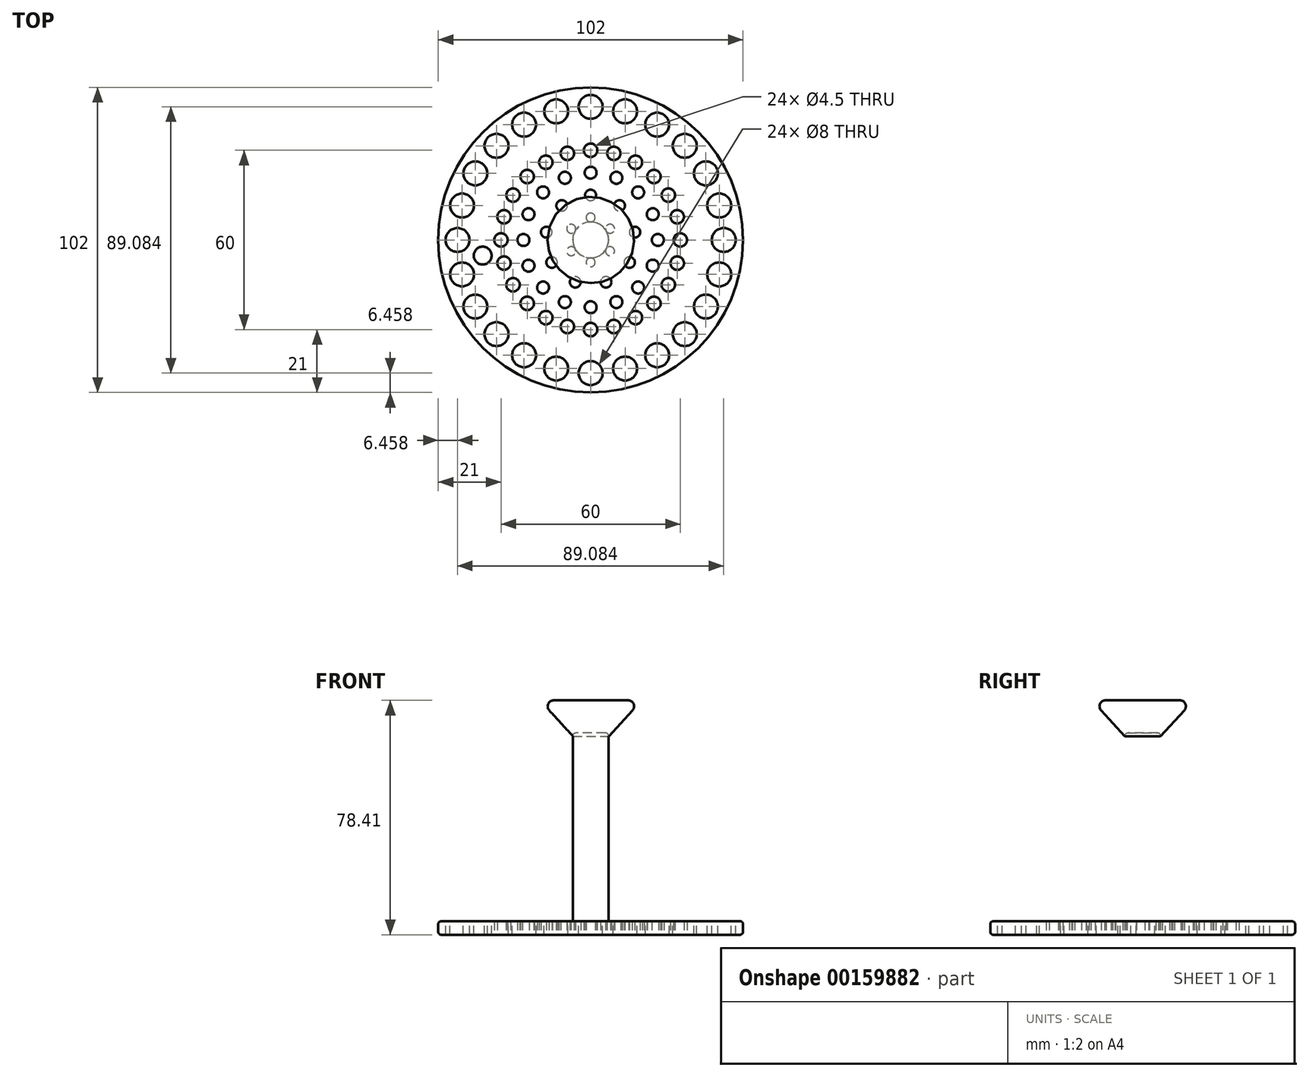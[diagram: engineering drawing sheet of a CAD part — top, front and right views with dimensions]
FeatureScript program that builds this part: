
annotation { "Feature Type Name" : "Feature", "Feature Type Description" : "" }
export const myFeature = defineFeature(function(context is Context, id is Id, definition is map)
    precondition{}
    {
        {
            var Q0;
            Q0=qCreatedBy(makeId("Top.planeOp"),FACE);
            var sketch = newSketch(context, id + "F0", { "sketchPlane" : qUnion([Q0])});
            skCircle(sketch, "E0", {"center": v(0, 0) * mm, "radius": 51 * mm});
            skSolve(sketch);
        }
        {
            var Q0;
            Q0=makeQuery(id+"F0.imprint","IMPRINT",FACE,{"disambiguationData":[TD([[makeQuery(id+"F0.imprint","IMPRINT",EDGE,{"derivedFrom":sQuery(id+"F0.wireOp",EDGE,"E0")}),1.0]])]});
            var sketch = newSketch(context, id + "F1", { "sketchPlane" : qUnion([Q0])});
            skCircle(sketch, "E1", {"center": v(0, 0) * mm, "radius": 7.5 * mm, "construction": true});
            skCircle(sketch, "E2", {"center": v(0, 7.5) * mm, "radius": 1.5 * mm});
            skCircle(sketch, "E3.1.1", {"center": v(-6.5, 3.75) * mm, "radius": 1.5 * mm});
            skCircle(sketch, "E3.2.1", {"center": v(-6.5, -3.75) * mm, "radius": 1.5 * mm});
            skCircle(sketch, "E3.3.1", {"center": v(0, -7.5) * mm, "radius": 1.5 * mm});
            skCircle(sketch, "E3.4.1", {"center": v(6.5, -3.75) * mm, "radius": 1.5 * mm});
            skCircle(sketch, "E3.5.1", {"center": v(6.5, 3.75) * mm, "radius": 1.5 * mm});
            skSolve(sketch);
        }
        {
            var Q0;
            Q0=makeQuery(id+"F0.imprint","IMPRINT",FACE,{"disambiguationData":[TD([[makeQuery(id+"F0.imprint","IMPRINT",EDGE,{"derivedFrom":sQuery(id+"F0.wireOp",EDGE,"E0")}),1.0]])]});
            var sketch = newSketch(context, id + "F2", { "sketchPlane" : qUnion([Q0])});
            skCircle(sketch, "E4", {"center": v(0, 0) * mm, "radius": 15 * mm, "construction": true});
            skCircle(sketch, "E5", {"center": v(0, 15) * mm, "radius": 1.83 * mm});
            skCircle(sketch, "E6.1.0", {"center": v(-9.64, 11.5) * mm, "radius": 1.83 * mm});
            skCircle(sketch, "E6.2.0", {"center": v(-14.77, 2.6) * mm, "radius": 1.83 * mm});
            skCircle(sketch, "E6.3.0", {"center": v(-13, -7.5) * mm, "radius": 1.83 * mm});
            skCircle(sketch, "E6.4.0", {"center": v(-5.13, -14.1) * mm, "radius": 1.83 * mm});
            skCircle(sketch, "E6.5.0", {"center": v(5.13, -14.1) * mm, "radius": 1.83 * mm});
            skCircle(sketch, "E6.6.0", {"center": v(13, -7.5) * mm, "radius": 1.83 * mm});
            skCircle(sketch, "E6.7.0", {"center": v(14.77, 2.6) * mm, "radius": 1.83 * mm});
            skCircle(sketch, "E6.8.0", {"center": v(9.64, 11.5) * mm, "radius": 1.83 * mm});
            skSolve(sketch);
        }
        {
            var Q0;
            Q0=makeQuery(id+"F0.imprint","IMPRINT",FACE,{"disambiguationData":[TD([[makeQuery(id+"F0.imprint","IMPRINT",EDGE,{"derivedFrom":sQuery(id+"F0.wireOp",EDGE,"E0")}),1.0]])]});
            var sketch = newSketch(context, id + "F3", { "sketchPlane" : qUnion([Q0])});
            skCircle(sketch, "E7", {"center": v(0, 0) * mm, "radius": 22.5 * mm, "construction": true});
            skCircle(sketch, "E8", {"center": v(0, 22.5) * mm, "radius": 2 * mm});
            skCircle(sketch, "E9.1.0", {"center": v(-8.61, 20.79) * mm, "radius": 2 * mm});
            skCircle(sketch, "E9.2.0", {"center": v(-15.9, 15.9) * mm, "radius": 2 * mm});
            skCircle(sketch, "E9.3.0", {"center": v(-20.79, 8.61) * mm, "radius": 2 * mm});
            skCircle(sketch, "E9.4.0", {"center": v(-22.5, 0) * mm, "radius": 2 * mm});
            skCircle(sketch, "E9.5.0", {"center": v(-20.79, -8.61) * mm, "radius": 2 * mm});
            skCircle(sketch, "E9.6.0", {"center": v(-15.9, -15.9) * mm, "radius": 2 * mm});
            skCircle(sketch, "E9.7.0", {"center": v(-8.61, -20.79) * mm, "radius": 2 * mm});
            skCircle(sketch, "E9.8.0", {"center": v(0, -22.5) * mm, "radius": 2 * mm});
            skCircle(sketch, "E9.9.0", {"center": v(8.61, -20.79) * mm, "radius": 2 * mm});
            skCircle(sketch, "E9.10.0", {"center": v(15.9, -15.9) * mm, "radius": 2 * mm});
            skCircle(sketch, "E9.11.0", {"center": v(20.79, -8.61) * mm, "radius": 2 * mm});
            skCircle(sketch, "E9.12.0", {"center": v(22.5, 0) * mm, "radius": 2 * mm});
            skCircle(sketch, "E9.13.0", {"center": v(20.79, 8.61) * mm, "radius": 2 * mm});
            skCircle(sketch, "E9.14.0", {"center": v(15.9, 15.9) * mm, "radius": 2 * mm});
            skCircle(sketch, "E9.15.0", {"center": v(8.61, 20.79) * mm, "radius": 2 * mm});
            skSolve(sketch);
        }
        {
            var Q0;
            Q0=makeQuery(id+"F0.imprint","IMPRINT",FACE,{"disambiguationData":[TD([[makeQuery(id+"F0.imprint","IMPRINT",EDGE,{"derivedFrom":sQuery(id+"F0.wireOp",EDGE,"E0")}),1.0]])]});
            var sketch = newSketch(context, id + "F4", { "sketchPlane" : qUnion([Q0])});
            skCircle(sketch, "E10", {"center": v(0, 0) * mm, "radius": 30 * mm, "construction": true});
            skCircle(sketch, "E11", {"center": v(0, 30) * mm, "radius": 2.25 * mm});
            skCircle(sketch, "E12.1.0", {"center": v(-7.76, 28.98) * mm, "radius": 2.25 * mm});
            skCircle(sketch, "E12.2.0", {"center": v(-15, 25.98) * mm, "radius": 2.25 * mm});
            skCircle(sketch, "E13.1.3.0", {"center": v(-21.21, 21.21) * mm, "radius": 2.25 * mm});
            skCircle(sketch, "E13.1.4.0", {"center": v(-25.98, 15) * mm, "radius": 2.25 * mm});
            skCircle(sketch, "E13.1.5.0", {"center": v(-28.98, 7.76) * mm, "radius": 2.25 * mm});
            skCircle(sketch, "E13.1.6.0", {"center": v(-30, 0) * mm, "radius": 2.25 * mm});
            skCircle(sketch, "E13.1.7.0", {"center": v(-28.98, -7.76) * mm, "radius": 2.25 * mm});
            skCircle(sketch, "E13.1.8.0", {"center": v(-25.98, -15) * mm, "radius": 2.25 * mm});
            skCircle(sketch, "E13.1.9.0", {"center": v(-21.21, -21.21) * mm, "radius": 2.25 * mm});
            skCircle(sketch, "E13.1.10.0", {"center": v(-15, -25.98) * mm, "radius": 2.25 * mm});
            skCircle(sketch, "E13.1.11.0", {"center": v(-7.76, -28.98) * mm, "radius": 2.25 * mm});
            skCircle(sketch, "E13.1.12.0", {"center": v(0, -30) * mm, "radius": 2.25 * mm});
            skCircle(sketch, "E13.1.13.0", {"center": v(7.76, -28.98) * mm, "radius": 2.25 * mm});
            skCircle(sketch, "E13.1.14.0", {"center": v(15, -25.98) * mm, "radius": 2.25 * mm});
            skCircle(sketch, "E13.1.15.0", {"center": v(21.21, -21.21) * mm, "radius": 2.25 * mm});
            skCircle(sketch, "E13.1.16.0", {"center": v(25.98, -15) * mm, "radius": 2.25 * mm});
            skCircle(sketch, "E13.1.17.0", {"center": v(28.98, -7.76) * mm, "radius": 2.25 * mm});
            skCircle(sketch, "E13.1.18.0", {"center": v(30, 0) * mm, "radius": 2.25 * mm});
            skCircle(sketch, "E13.1.19.0", {"center": v(28.98, 7.76) * mm, "radius": 2.25 * mm});
            skCircle(sketch, "E13.1.20.0", {"center": v(25.98, 15) * mm, "radius": 2.25 * mm});
            skCircle(sketch, "E13.1.21.0", {"center": v(21.21, 21.21) * mm, "radius": 2.25 * mm});
            skCircle(sketch, "E13.1.22.0", {"center": v(15, 25.98) * mm, "radius": 2.25 * mm});
            skCircle(sketch, "E13.1.23.0", {"center": v(7.76, 28.98) * mm, "radius": 2.25 * mm});
            skSolve(sketch);
        }
        {
            var Q0;
            Q0=qSketchRegion(id+"F4",true);
            extrude(context, id + "F5", {"entities" : qUnion([Q0]), "depth" : 5 * mm});
        }
        {
            var Q0;
            Q0=qSketchRegion(id+"F3",true);
            extrude(context, id + "F6", {"entities" : qUnion([Q0]), "depth" : 5 * mm});
        }
        {
            var Q0;
            Q0=qSketchRegion(id+"F2",true);
            extrude(context, id + "F7", {"entities" : qUnion([Q0]), "depth" : 5 * mm});
        }
        {
            var Q0;
            Q0=qSketchRegion(id+"F1",true);
            extrude(context, id + "F8", {"entities" : qUnion([Q0]), "depth" : 5 * mm});
        }
        {
            var Q0;
            Q0=qSketchRegion(id+"F0",true);
            extrude(context, id + "F9", {"entities" : qUnion([Q0]), "depth" : 4.5 * mm});
        }
        {
            var Q0;
            Q0=makeQuery(id+"F5.opExtrude","SWEPT_BODY",BODY,{"disambiguationData":[OSD([sQuery(id+"F4.wireOp",EDGE,"E11")])]});
            var Q1;
            Q1=makeQuery(id+"F5.opExtrude","SWEPT_BODY",BODY,{"disambiguationData":[OSD([sQuery(id+"F4.wireOp",EDGE,"E13.1.3.0")])]});
            var Q2;
            Q2=makeQuery(id+"F5.opExtrude","SWEPT_BODY",BODY,{"disambiguationData":[OSD([sQuery(id+"F4.wireOp",EDGE,"E13.1.7.0")])]});
            var Q3;
            Q3=makeQuery(id+"F5.opExtrude","SWEPT_BODY",BODY,{"disambiguationData":[OSD([sQuery(id+"F4.wireOp",EDGE,"E12.1.0")])]});
            var Q4;
            Q4=makeQuery(id+"F5.opExtrude","SWEPT_BODY",BODY,{"disambiguationData":[OSD([sQuery(id+"F4.wireOp",EDGE,"E12.2.0")])]});
            var Q5;
            Q5=makeQuery(id+"F5.opExtrude","SWEPT_BODY",BODY,{"disambiguationData":[OSD([sQuery(id+"F4.wireOp",EDGE,"E13.1.4.0")])]});
            var Q6;
            Q6=makeQuery(id+"F5.opExtrude","SWEPT_BODY",BODY,{"disambiguationData":[OSD([sQuery(id+"F4.wireOp",EDGE,"E13.1.5.0")])]});
            var Q7;
            Q7=makeQuery(id+"F5.opExtrude","SWEPT_BODY",BODY,{"disambiguationData":[OSD([sQuery(id+"F4.wireOp",EDGE,"E13.1.6.0")])]});
            var Q8;
            Q8=makeQuery(id+"F5.opExtrude","SWEPT_BODY",BODY,{"disambiguationData":[OSD([sQuery(id+"F4.wireOp",EDGE,"E13.1.8.0")])]});
            var Q9;
            Q9=makeQuery(id+"F5.opExtrude","SWEPT_BODY",BODY,{"disambiguationData":[OSD([sQuery(id+"F4.wireOp",EDGE,"E13.1.9.0")])]});
            var Q10;
            Q10=makeQuery(id+"F5.opExtrude","SWEPT_BODY",BODY,{"disambiguationData":[OSD([sQuery(id+"F4.wireOp",EDGE,"E13.1.10.0")])]});
            var Q11;
            Q11=makeQuery(id+"F5.opExtrude","SWEPT_BODY",BODY,{"disambiguationData":[OSD([sQuery(id+"F4.wireOp",EDGE,"E13.1.11.0")])]});
            var Q12;
            Q12=makeQuery(id+"F5.opExtrude","SWEPT_BODY",BODY,{"disambiguationData":[OSD([sQuery(id+"F4.wireOp",EDGE,"E13.1.12.0")])]});
            var Q13;
            Q13=makeQuery(id+"F5.opExtrude","SWEPT_BODY",BODY,{"disambiguationData":[OSD([sQuery(id+"F4.wireOp",EDGE,"E13.1.13.0")])]});
            var Q14;
            Q14=makeQuery(id+"F5.opExtrude","SWEPT_BODY",BODY,{"disambiguationData":[OSD([sQuery(id+"F4.wireOp",EDGE,"E13.1.14.0")])]});
            var Q15;
            Q15=makeQuery(id+"F5.opExtrude","SWEPT_BODY",BODY,{"disambiguationData":[OSD([sQuery(id+"F4.wireOp",EDGE,"E13.1.15.0")])]});
            var Q16;
            Q16=makeQuery(id+"F5.opExtrude","SWEPT_BODY",BODY,{"disambiguationData":[OSD([sQuery(id+"F4.wireOp",EDGE,"E13.1.16.0")])]});
            var Q17;
            Q17=makeQuery(id+"F5.opExtrude","SWEPT_BODY",BODY,{"disambiguationData":[OSD([sQuery(id+"F4.wireOp",EDGE,"E13.1.17.0")])]});
            var Q18;
            Q18=makeQuery(id+"F5.opExtrude","SWEPT_BODY",BODY,{"disambiguationData":[OSD([sQuery(id+"F4.wireOp",EDGE,"E13.1.18.0")])]});
            var Q19;
            Q19=makeQuery(id+"F5.opExtrude","SWEPT_BODY",BODY,{"disambiguationData":[OSD([sQuery(id+"F4.wireOp",EDGE,"E13.1.19.0")])]});
            var Q20;
            Q20=makeQuery(id+"F5.opExtrude","SWEPT_BODY",BODY,{"disambiguationData":[OSD([sQuery(id+"F4.wireOp",EDGE,"E13.1.20.0")])]});
            var Q21;
            Q21=makeQuery(id+"F5.opExtrude","SWEPT_BODY",BODY,{"disambiguationData":[OSD([sQuery(id+"F4.wireOp",EDGE,"E13.1.21.0")])]});
            var Q22;
            Q22=makeQuery(id+"F5.opExtrude","SWEPT_BODY",BODY,{"disambiguationData":[OSD([sQuery(id+"F4.wireOp",EDGE,"E13.1.22.0")])]});
            var Q23;
            Q23=makeQuery(id+"F5.opExtrude","SWEPT_BODY",BODY,{"disambiguationData":[OSD([sQuery(id+"F4.wireOp",EDGE,"E13.1.23.0")])]});
            var Q24;
            Q24=makeQuery(id+"F6.opExtrude","SWEPT_BODY",BODY,{"disambiguationData":[OSD([sQuery(id+"F3.wireOp",EDGE,"E9.15.0")])]});
            var Q25;
            Q25=makeQuery(id+"F6.opExtrude","SWEPT_BODY",BODY,{"disambiguationData":[OSD([sQuery(id+"F3.wireOp",EDGE,"E8")])]});
            var Q26;
            Q26=makeQuery(id+"F6.opExtrude","SWEPT_BODY",BODY,{"disambiguationData":[OSD([sQuery(id+"F3.wireOp",EDGE,"E9.1.0")])]});
            var Q27;
            Q27=makeQuery(id+"F6.opExtrude","SWEPT_BODY",BODY,{"disambiguationData":[OSD([sQuery(id+"F3.wireOp",EDGE,"E9.2.0")])]});
            var Q28;
            Q28=makeQuery(id+"F6.opExtrude","SWEPT_BODY",BODY,{"disambiguationData":[OSD([sQuery(id+"F3.wireOp",EDGE,"E9.3.0")])]});
            var Q29;
            Q29=makeQuery(id+"F6.opExtrude","SWEPT_BODY",BODY,{"disambiguationData":[OSD([sQuery(id+"F3.wireOp",EDGE,"E9.4.0")])]});
            var Q30;
            Q30=makeQuery(id+"F6.opExtrude","SWEPT_BODY",BODY,{"disambiguationData":[OSD([sQuery(id+"F3.wireOp",EDGE,"E9.5.0")])]});
            var Q31;
            Q31=makeQuery(id+"F6.opExtrude","SWEPT_BODY",BODY,{"disambiguationData":[OSD([sQuery(id+"F3.wireOp",EDGE,"E9.6.0")])]});
            var Q32;
            Q32=makeQuery(id+"F6.opExtrude","SWEPT_BODY",BODY,{"disambiguationData":[OSD([sQuery(id+"F3.wireOp",EDGE,"E9.7.0")])]});
            var Q33;
            Q33=makeQuery(id+"F6.opExtrude","SWEPT_BODY",BODY,{"disambiguationData":[OSD([sQuery(id+"F3.wireOp",EDGE,"E9.8.0")])]});
            var Q34;
            Q34=makeQuery(id+"F6.opExtrude","SWEPT_BODY",BODY,{"disambiguationData":[OSD([sQuery(id+"F3.wireOp",EDGE,"E9.9.0")])]});
            var Q35;
            Q35=makeQuery(id+"F6.opExtrude","SWEPT_BODY",BODY,{"disambiguationData":[OSD([sQuery(id+"F3.wireOp",EDGE,"E9.10.0")])]});
            var Q36;
            Q36=makeQuery(id+"F6.opExtrude","SWEPT_BODY",BODY,{"disambiguationData":[OSD([sQuery(id+"F3.wireOp",EDGE,"E9.11.0")])]});
            var Q37;
            Q37=makeQuery(id+"F6.opExtrude","SWEPT_BODY",BODY,{"disambiguationData":[OSD([sQuery(id+"F3.wireOp",EDGE,"E9.12.0")])]});
            var Q38;
            Q38=makeQuery(id+"F6.opExtrude","SWEPT_BODY",BODY,{"disambiguationData":[OSD([sQuery(id+"F3.wireOp",EDGE,"E9.13.0")])]});
            var Q39;
            Q39=makeQuery(id+"F6.opExtrude","SWEPT_BODY",BODY,{"disambiguationData":[OSD([sQuery(id+"F3.wireOp",EDGE,"E9.14.0")])]});
            var Q40;
            Q40=makeQuery(id+"F7.opExtrude","SWEPT_BODY",BODY,{"disambiguationData":[OSD([sQuery(id+"F2.wireOp",EDGE,"E6.8.0")])]});
            var Q41;
            Q41=makeQuery(id+"F7.opExtrude","SWEPT_BODY",BODY,{"disambiguationData":[OSD([sQuery(id+"F2.wireOp",EDGE,"E6.7.0")])]});
            var Q42;
            Q42=makeQuery(id+"F7.opExtrude","SWEPT_BODY",BODY,{"disambiguationData":[OSD([sQuery(id+"F2.wireOp",EDGE,"E6.6.0")])]});
            var Q43;
            Q43=makeQuery(id+"F7.opExtrude","SWEPT_BODY",BODY,{"disambiguationData":[OSD([sQuery(id+"F2.wireOp",EDGE,"E6.5.0")])]});
            var Q44;
            Q44=makeQuery(id+"F7.opExtrude","SWEPT_BODY",BODY,{"disambiguationData":[OSD([sQuery(id+"F2.wireOp",EDGE,"E6.4.0")])]});
            var Q45;
            Q45=makeQuery(id+"F7.opExtrude","SWEPT_BODY",BODY,{"disambiguationData":[OSD([sQuery(id+"F2.wireOp",EDGE,"E6.3.0")])]});
            var Q46;
            Q46=makeQuery(id+"F7.opExtrude","SWEPT_BODY",BODY,{"disambiguationData":[OSD([sQuery(id+"F2.wireOp",EDGE,"E6.2.0")])]});
            var Q47;
            Q47=makeQuery(id+"F7.opExtrude","SWEPT_BODY",BODY,{"disambiguationData":[OSD([sQuery(id+"F2.wireOp",EDGE,"E6.1.0")])]});
            var Q48;
            Q48=makeQuery(id+"F7.opExtrude","SWEPT_BODY",BODY,{"disambiguationData":[OSD([sQuery(id+"F2.wireOp",EDGE,"E5")])]});
            var Q49;
            Q49=makeQuery(id+"F8.opExtrude","SWEPT_BODY",BODY,{"disambiguationData":[OSD([sQuery(id+"F1.wireOp",EDGE,"E2")])]});
            var Q50;
            Q50=makeQuery(id+"F8.opExtrude","SWEPT_BODY",BODY,{"disambiguationData":[OSD([sQuery(id+"F1.wireOp",EDGE,"E3.5.1")])]});
            var Q51;
            Q51=makeQuery(id+"F8.opExtrude","SWEPT_BODY",BODY,{"disambiguationData":[OSD([sQuery(id+"F1.wireOp",EDGE,"E3.4.1")])]});
            var Q52;
            Q52=makeQuery(id+"F8.opExtrude","SWEPT_BODY",BODY,{"disambiguationData":[OSD([sQuery(id+"F1.wireOp",EDGE,"E3.3.1")])]});
            var Q53;
            Q53=makeQuery(id+"F8.opExtrude","SWEPT_BODY",BODY,{"disambiguationData":[OSD([sQuery(id+"F1.wireOp",EDGE,"E3.2.1")])]});
            var Q54;
            Q54=makeQuery(id+"F8.opExtrude","SWEPT_BODY",BODY,{"disambiguationData":[OSD([sQuery(id+"F1.wireOp",EDGE,"E3.1.1")])]});
            var Q55;
            Q55=makeQuery(id+"F9.opExtrude","SWEPT_BODY",BODY,{"disambiguationData":[OSD([sQuery(id+"F0.wireOp",EDGE,"E0")])]});
            booleanBodies(context, id + "F10", {"operationType" : BooleanOperationType.SUBTRACTION, "tools" : qUnion([Q0, Q1, Q2, Q3, Q4, Q5, Q6, Q7, Q8, Q9, Q10, Q11, Q12, Q13, Q14, Q15, Q16, Q17, Q18, Q19, Q20, Q21, Q22, Q23, Q24, Q25, Q26, Q27, Q28, Q29, Q30, Q31, Q32, Q33, Q34, Q35, Q36, Q37, Q38, Q39, Q40, Q41, Q42, Q43, Q44, Q45, Q46, Q47, Q48, Q49, Q50, Q51, Q52, Q53, Q54]), "targets" : qUnion([Q55])});
        }
        {
            var Q0;
            Q0=makeQuery(id+"F9.opExtrude","CAP_EDGE",EDGE,{"disambiguationData":[OSD([sQuery(id+"F0.wireOp",EDGE,"E0")])],"isStart":true});
            var Q1;
            Q1=makeQuery(id+"F9.opExtrude","CAP_EDGE",EDGE,{"disambiguationData":[OSD([sQuery(id+"F0.wireOp",EDGE,"E0")])],"isStart":false});
            fillet(context, id + "F11", {"entities" : qUnion([Q0, Q1]), "radius" : 1 * mm, "tangentPropagation" : true, "allowEdgeOverflow" : false});
        }
        {
            var Q0;
            Q0=makeQuery(id+"F9.opExtrude","CAP_FACE",FACE,{"disambiguationData":[OSD([sQuery(id+"F0.wireOp",EDGE,"E0")])],"isStart":false});
            var sketch = newSketch(context, id + "F12", { "sketchPlane" : qUnion([Q0])});
            skCircle(sketch, "E14", {"center": v(0, 0) * mm, "radius": 6 * mm});
            skSolve(sketch);
        }
        {
            var Q0;
            Q0=makeQuery(id+"F12.imprint","IMPRINT",FACE,{"disambiguationData":[TD([[makeQuery(id+"F12.imprint","IMPRINT",EDGE,{"derivedFrom":sQuery(id+"F12.wireOp",EDGE,"E14")}),1.0]])]});
            extrude(context, id + "F13", {"entities" : qUnion([Q0]), "operationType" : NewBodyOperationType.ADD, "offsetDistance" : 25 * mm, "depth" : 63 * mm});
        }
        {
            var Q0;
            Q0=makeQuery(id+"F13.opExtrude","CAP_EDGE",EDGE,{"disambiguationData":[OSD([sQuery(id+"F12.wireOp",EDGE,"E14")])],"isStart":false});
            fillet(context, id + "F14", {"entities" : qUnion([Q0]), "radius" : 1 * mm, "tangentPropagation" : true, "allowEdgeOverflow" : false});
        }
        {
            var Q0;
            Q0=makeQuery(id+"F9.opExtrude","CAP_FACE",FACE,{"disambiguationData":[OSD([sQuery(id+"F0.wireOp",EDGE,"E0")])],"isStart":false});
            var sketch = newSketch(context, id + "F15", { "sketchPlane" : qUnion([Q0])});
            skCircle(sketch, "E15", {"center": v(0, 0) * mm, "radius": 36.5 * mm, "construction": true});
            skCircle(sketch, "E16", {"center": v(-36.12, -5.23) * mm, "radius": 3 * mm});
            skSolve(sketch);
        }
        {
            var Q0;
            Q0=makeQuery(id+"F15.imprint","IMPRINT",FACE,{"disambiguationData":[TD([[makeQuery(id+"F15.imprint","IMPRINT",EDGE,{"derivedFrom":sQuery(id+"F15.wireOp",EDGE,"E16")}),1.0]])]});
            extrude(context, id + "F16", {"entities" : qUnion([Q0]), "operationType" : NewBodyOperationType.REMOVE, "oppositeDirection" : true, "offsetDistance" : 25 * mm, "depth" : 25 * mm});
        }
        {
            var Q0;
            Q0=makeQuery(id+"F9.opExtrude","CAP_FACE",FACE,{"disambiguationData":[OSD([sQuery(id+"F0.wireOp",EDGE,"E0")])],"isStart":false});
            var sketch = newSketch(context, id + "F17", { "sketchPlane" : qUnion([Q0])});
            skCircle(sketch, "E17", {"center": v(0, 0) * mm, "radius": 4.85 * mm, "construction": true});
            skCircle(sketch, "E18", {"center": v(0, 0) * mm, "radius": 44.54 * mm, "construction": true});
            skCircle(sketch, "E19", {"center": v(-44.54, 0) * mm, "radius": 4 * mm});
            skCircle(sketch, "E20.1.0", {"center": v(-43.02, -11.53) * mm, "radius": 4 * mm});
            skCircle(sketch, "E20.2.0", {"center": v(-38.57, -22.27) * mm, "radius": 4 * mm});
            skCircle(sketch, "E20.3.0", {"center": v(-31.5, -31.5) * mm, "radius": 4 * mm});
            skCircle(sketch, "E20.4.0", {"center": v(-22.27, -38.57) * mm, "radius": 4 * mm});
            skCircle(sketch, "E20.5.0", {"center": v(-11.53, -43.02) * mm, "radius": 4 * mm});
            skCircle(sketch, "E20.6.0", {"center": v(0, -44.54) * mm, "radius": 4 * mm});
            skCircle(sketch, "E20.7.0", {"center": v(11.53, -43.02) * mm, "radius": 4 * mm});
            skCircle(sketch, "E20.8.0", {"center": v(22.27, -38.57) * mm, "radius": 4 * mm});
            skCircle(sketch, "E20.9.0", {"center": v(31.5, -31.5) * mm, "radius": 4 * mm});
            skCircle(sketch, "E20.10.0", {"center": v(38.57, -22.27) * mm, "radius": 4 * mm});
            skCircle(sketch, "E20.11.0", {"center": v(43.02, -11.53) * mm, "radius": 4 * mm});
            skCircle(sketch, "E20.12.0", {"center": v(44.54, 0) * mm, "radius": 4 * mm});
            skCircle(sketch, "E20.13.0", {"center": v(43.02, 11.53) * mm, "radius": 4 * mm});
            skCircle(sketch, "E20.14.0", {"center": v(38.57, 22.27) * mm, "radius": 4 * mm});
            skCircle(sketch, "E20.15.0", {"center": v(31.5, 31.5) * mm, "radius": 4 * mm});
            skCircle(sketch, "E20.16.0", {"center": v(22.27, 38.57) * mm, "radius": 4 * mm});
            skCircle(sketch, "E20.17.0", {"center": v(11.53, 43.02) * mm, "radius": 4 * mm});
            skCircle(sketch, "E20.18.0", {"center": v(0, 44.54) * mm, "radius": 4 * mm});
            skCircle(sketch, "E20.19.0", {"center": v(-11.53, 43.02) * mm, "radius": 4 * mm});
            skCircle(sketch, "E20.20.0", {"center": v(-22.27, 38.57) * mm, "radius": 4 * mm});
            skCircle(sketch, "E20.21.0", {"center": v(-31.5, 31.5) * mm, "radius": 4 * mm});
            skCircle(sketch, "E20.22.0", {"center": v(-38.57, 22.27) * mm, "radius": 4 * mm});
            skCircle(sketch, "E20.23.0", {"center": v(-43.02, 11.53) * mm, "radius": 4 * mm});
            skSolve(sketch);
        }
        {
            var Q0;
            Q0 = qSketchRegion(id + "F17", true);
            extrude(context, id + "F18", {"entities" : qUnion([Q0]), "operationType" : NewBodyOperationType.REMOVE, "endBound" : BoundingType.THROUGH_ALL, "oppositeDirection" : true, "depth" : 25 * mm, "offsetDistance" : 25 * mm});
        }
        {
            var Q0;
            Q0=qCreatedBy(makeId("Front.planeOp"),FACE);
            var sketch = newSketch(context, id + "F19", { "sketchPlane" : qUnion([Q0])});
            skLineSegment(sketch, "E21", {"start": v(0.07, 59.13) * mm, "end": v(0.07, 79.6) * mm, "construction": true});
            skLineSegment(sketch, "E22", {"start": v(0.07, 79.6) * mm, "end": v(-16.93, 79.6) * mm});
            skLineSegment(sketch, "E23", {"start": v(-16.93, 79.6) * mm, "end": v(-5.93, 67.6) * mm});
            skLineSegment(sketch, "E24", {"start": v(-5.93, 67.6) * mm, "end": v(0.07, 67.6) * mm});
            skLineSegment(sketch, "E25", {"start": v(0.07, 67.6) * mm, "end": v(0.07, 79.6) * mm});
            skSolve(sketch);
        }
        {
            var Q0;
            Q0 = qSketchRegion(id + "F19", true);
            var Q1;
            Q1=sQuery(id+"F19.wireOp",EDGE,"E21");
            revolve(context, id + "F20", {"surfaceOperationType" : NewSurfaceOperationType.NEW, "entities" : qUnion([Q0]), "axis" : qUnion([Q1]), "revolveType" : RevolveType.FULL});
        }
        {
            var Q0;
            Q0=makeQuery(id+"F20.opRevolve","SWEPT_BODY",BODY,{"disambiguationData":[OSD([sQuery(id+"F19.wireOp",EDGE,"E22"),sQuery(id+"F19.wireOp",EDGE,"E23"),sQuery(id+"F19.wireOp",EDGE,"E24"),sQuery(id+"F19.wireOp",EDGE,"E25")])]});
            transform(context, id + "F21", {"entities" : qUnion([Q0]), "transformType" : TransformType.TRANSLATION_3D, "dx" : 0 * mm, "dy" : 0 * mm, "dz" : -1.2 * mm, "makeCopy" : false});
        }
        {
            var Q0;
            Q0=makeQuery(id+"F20.opRevolve","SWEPT_EDGE",EDGE,{"disambiguationData":[OSD([sQuery(id+"F19.wireOp",EDGE,"E22"),sQuery(id+"F19.wireOp",EDGE,"E23")])]});
            fillet(context, id + "F22", {"entities" : qUnion([Q0]), "radius" : 2 * mm, "tangentPropagation" : true, "allowEdgeOverflow" : false});
        }
    });
